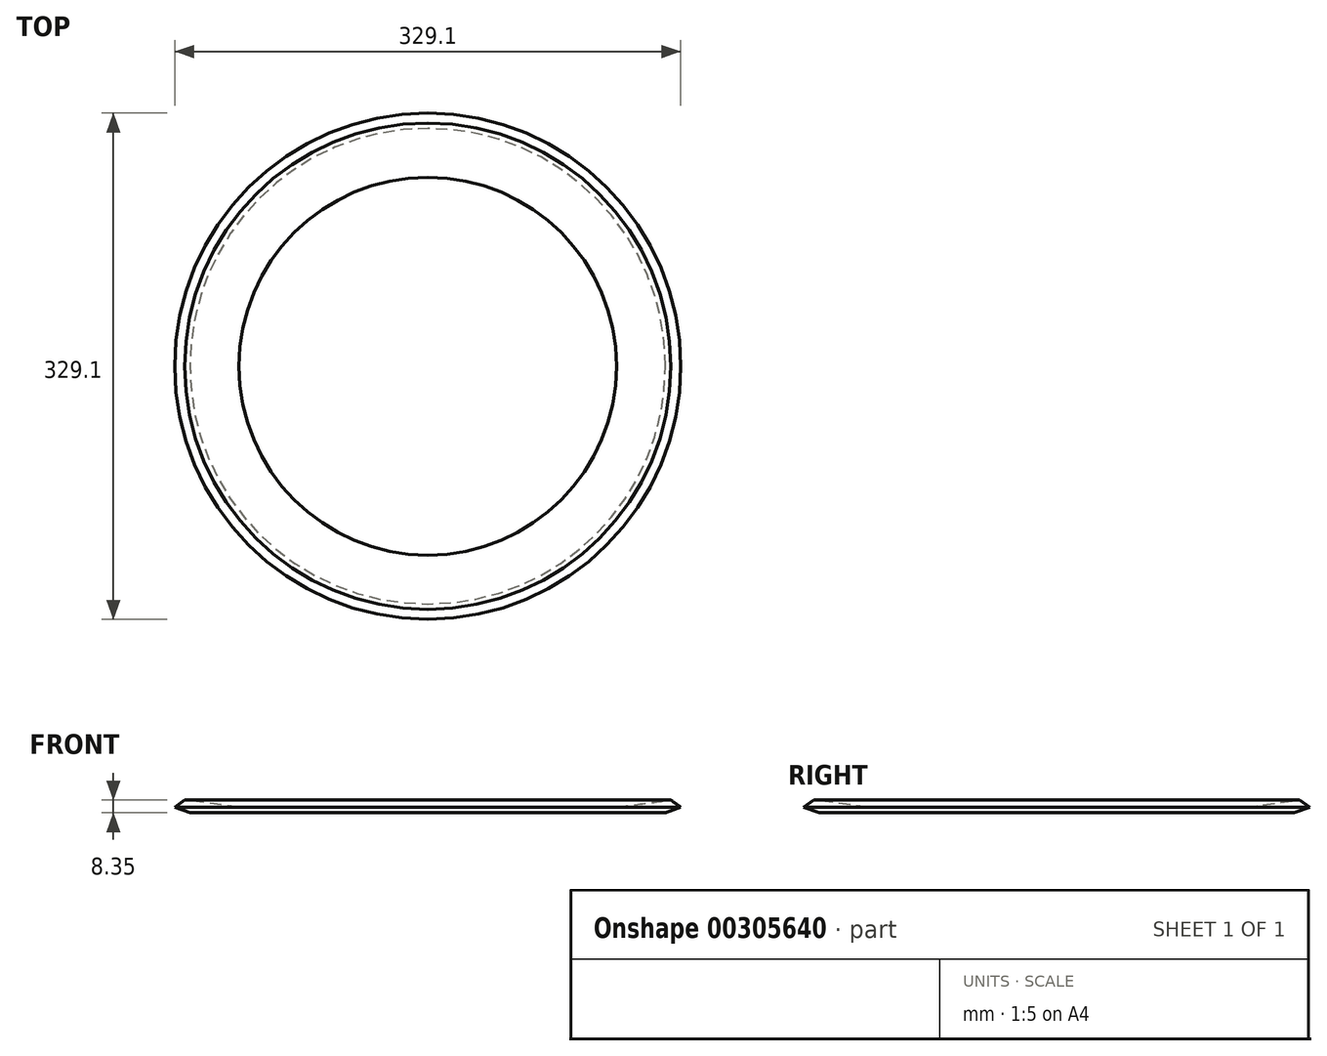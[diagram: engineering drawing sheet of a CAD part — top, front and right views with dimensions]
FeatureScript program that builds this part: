
annotation { "Feature Type Name" : "Feature", "Feature Type Description" : "" }
export const myFeature = defineFeature(function(context is Context, id is Id, definition is map)
    precondition{}
    {
        {
            var Q0;
            Q0=qCreatedBy(makeId("Front.planeOp"),FACE);
            var sketch = newSketch(context, id + "F0", { "sketchPlane" : qUnion([Q0])});
            skLineSegment(sketch, "E0", {"start": v(4.62, 0) * mm, "end": v(154.62, 0) * mm});
            skLineSegment(sketch, "E1", {"start": v(154.62, 0) * mm, "end": v(164.55, 3.65) * mm});
            skLineSegment(sketch, "E2", {"start": v(164.55, 3.65) * mm, "end": v(158.1, 8.35) * mm});
            skLineSegment(sketch, "E3", {"start": v(158.1, 8.35) * mm, "end": v(122.83, 3.65) * mm});
            skLineSegment(sketch, "E4", {"start": v(122.83, 3.65) * mm, "end": v(0, 3.65) * mm});
            skLineSegment(sketch, "E5", {"start": v(5.54, 0) * mm, "end": v(0, 0) * mm});
            skLineSegment(sketch, "E6", {"start": v(0, 3.65) * mm, "end": v(0, 0) * mm});
            skSolve(sketch);
        }
        {
            var Q0;
            Q0 = qSketchRegion(id + "F0", true);
            var Q1;
            Q1=sQuery(id+"F0.wireOp",EDGE,"E6");
            revolve(context, id + "F1", {"entities" : qUnion([Q0]), "axis" : qUnion([Q1]), "revolveType" : RevolveType.FULL});
        }
    });
